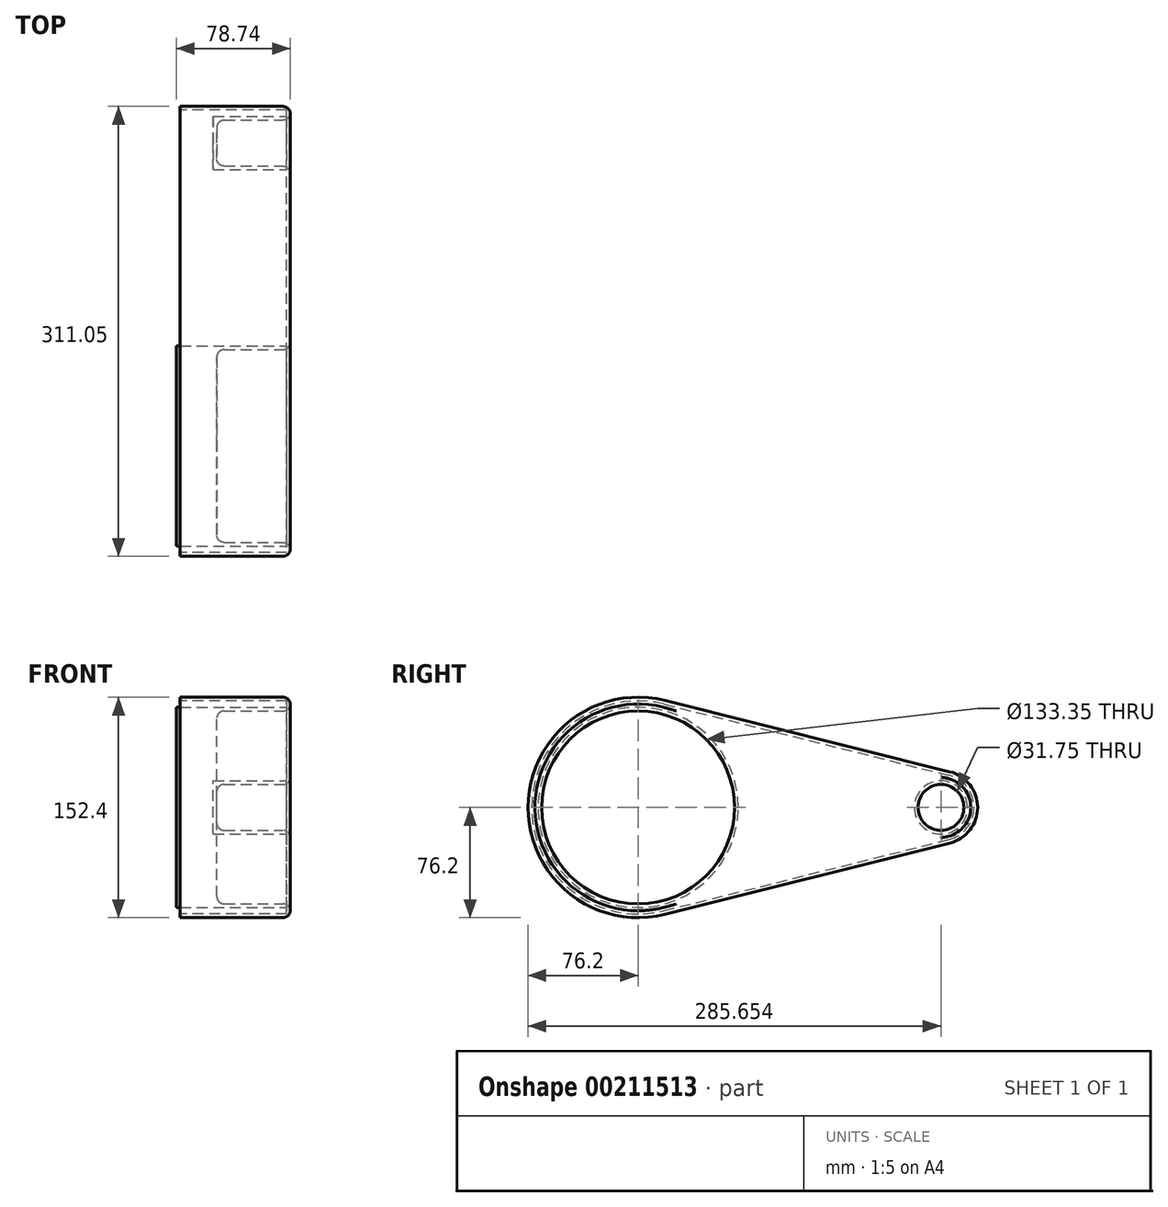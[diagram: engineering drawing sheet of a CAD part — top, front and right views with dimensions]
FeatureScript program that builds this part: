
annotation { "Feature Type Name" : "Feature", "Feature Type Description" : "" }
export const myFeature = defineFeature(function(context is Context, id is Id, definition is map)
    precondition{}
    {
        {
            var Q0;
            Q0=qCreatedBy(makeId("Right.planeOp"),FACE);
            var sketch = newSketch(context, id + "F0", { "sketchPlane" : qUnion([Q0])});
            skCircle(sketch, "E0", {"center": v(0, 0) * mm, "radius": 76.2 * mm});
            skCircle(sketch, "E1", {"center": v(209.45, 0) * mm, "radius": 25.4 * mm});
            skLineSegment(sketch, "E2", {"start": v(18.48, 73.92) * mm, "end": v(215.61, 24.64) * mm});
            skLineSegment(sketch, "E3", {"start": v(18.48, -73.92) * mm, "end": v(215.61, -24.64) * mm});
            skSolve(sketch);
        }
        {
            var Q0;
            {var subQ0=sQuery(id+"F0.wireOp",EDGE,"E2");Q0=makeQuery(id+"F0.imprint","IMPRINT",FACE,{"disambiguationData":[TD([[makeQuery(id+"F0.imprint","IMPRINT",EDGE,{"derivedFrom":subQ0}),-1.0]])]});}
            var Q1;
            {var subQ0=sQuery(id+"F0.wireOp",EDGE,"E0");var subQ1=makeQuery(id+"F0.imprint","INTERSECT",VERTEX,{"derivedFrom":[subQ0,sQuery(id+"F0.wireOp",EDGE,"E2")]});Q1=makeQuery(id+"F0.imprint","IMPRINT",FACE,{"disambiguationData":[TD([[makeQuery(id+"F0.imprint","IMPRINT",EDGE,{"disambiguationData":[TD([[subQ1,-1.0]])],"derivedFrom":subQ0}),1.0]])]});}
            var Q2;
            {var subQ0=sQuery(id+"F0.wireOp",EDGE,"E1");var subQ1=makeQuery(id+"F0.imprint","INTERSECT",VERTEX,{"derivedFrom":[subQ0,sQuery(id+"F0.wireOp",EDGE,"E2")]});Q2=makeQuery(id+"F0.imprint","IMPRINT",FACE,{"disambiguationData":[TD([[makeQuery(id+"F0.imprint","IMPRINT",EDGE,{"disambiguationData":[TD([[subQ1,-1.0]])],"derivedFrom":subQ0}),1.0]])]});}
            extrude(context, id + "F1", {"entities" : qUnion([Q0, Q1, Q2]), "depth" : 76.2 * mm});
        }
        {
            var Q0;
            Q0=makeQuery(id+"F1.opExtrude","CAP_FACE",FACE,{"disambiguationData":[OSD([sQuery(id+"F0.wireOp",EDGE,"E0"),sQuery(id+"F0.wireOp",EDGE,"E1"),sQuery(id+"F0.wireOp",EDGE,"E2"),sQuery(id+"F0.wireOp",EDGE,"E3")])],"isStart":false});
            var sketch = newSketch(context, id + "F2", { "sketchPlane" : qUnion([Q0])});
            skCircle(sketch, "E4", {"center": v(0, 0) * mm, "radius": 66.68 * mm});
            skCircle(sketch, "E5", {"center": v(209.45, 0) * mm, "radius": 15.88 * mm});
            skSolve(sketch);
        }
        {
            var Q0;
            Q0=makeQuery(id+"F2.imprint","IMPRINT",FACE,{"disambiguationData":[TD([[makeQuery(id+"F2.imprint","IMPRINT",EDGE,{"derivedFrom":sQuery(id+"F2.wireOp",EDGE,"E4")}),1.0]])]});
            extrude(context, id + "F3", {"entities" : qUnion([Q0]), "operationType" : NewBodyOperationType.REMOVE, "oppositeDirection" : true, "depth" : 50.8 * mm});
        }
        {
            var Q0;
            Q0=makeQuery(id+"F2.imprint","IMPRINT",FACE,{"disambiguationData":[TD([[makeQuery(id+"F2.imprint","IMPRINT",EDGE,{"derivedFrom":sQuery(id+"F2.wireOp",EDGE,"E5")}),1.0]])]});
            extrude(context, id + "F4", {"entities" : qUnion([Q0]), "operationType" : NewBodyOperationType.REMOVE, "oppositeDirection" : true, "depth" : 50.8 * mm});
        }
        {
            var Q0;
            Q0=makeQuery(id+"F1.opExtrude","CAP_FACE",FACE,{"disambiguationData":[OSD([sQuery(id+"F0.wireOp",EDGE,"E0"),sQuery(id+"F0.wireOp",EDGE,"E1"),sQuery(id+"F0.wireOp",EDGE,"E2"),sQuery(id+"F0.wireOp",EDGE,"E3")])],"isStart":true});
            shell(context, id + "F5", {"entities" : qUnion([Q0]), "thickness" : 2.54 * mm});
        }
        {
            var Q0;
            Q0=makeQuery(id+"F1.opExtrude","CAP_FACE",FACE,{"disambiguationData":[OSD([sQuery(id+"F0.wireOp",EDGE,"E0"),sQuery(id+"F0.wireOp",EDGE,"E1"),sQuery(id+"F0.wireOp",EDGE,"E2"),sQuery(id+"F0.wireOp",EDGE,"E3")])],"isStart":false});
            fillet(context, id + "F6", {"entities" : qUnion([Q0]), "radius" : 5.08 * mm, "tangentPropagation" : true, "allowEdgeOverflow" : false});
        }
        {
            var Q0;
            Q0=makeQuery(id+"F3.boolean.opBoolean","COPY",FACE,{"derivedFrom":makeQuery(id+"F3.opExtrude","CAP_FACE",FACE,{"disambiguationData":[OSD([sQuery(id+"F2.wireOp",EDGE,"E4")])],"isStart":false})});
            var Q1;
            Q1=makeQuery(id+"F4.boolean.opBoolean","COPY",FACE,{"derivedFrom":makeQuery(id+"F4.opExtrude","CAP_FACE",FACE,{"disambiguationData":[OSD([sQuery(id+"F2.wireOp",EDGE,"E5")])],"isStart":false})});
            fillet(context, id + "F7", {"entities" : qUnion([Q0, Q1]), "radius" : 5.08 * mm, "tangentPropagation" : true, "allowEdgeOverflow" : false});
        }
        {
            var Q0;
            {var subQ0=sQuery(id+"F2.wireOp",EDGE,"E4");Q0=makeQuery(id+"F5.opShell","OFFSET_FACE",FACE,{"disambiguationData":[OSD([subQ0]),TDD([makeQuery(id+"F3.boolean.opBoolean","COPY",FACE,{"derivedFrom":makeQuery(id+"F3.opExtrude","CAP_FACE",FACE,{"disambiguationData":[OSD([subQ0])],"isStart":false})})])]});}
            extrude(context, id + "F8", {"entities" : qUnion([Q0]), "operationType" : NewBodyOperationType.ADD, "depth" : 25.4 * mm});
        }
    });
